# Revit family: Electrical_Equipment-Bridge_Module-HCS-NXHNB_Series
name_source: partatom
category: Data Devices
revit_build: Autodesk Revit 2014 (Build: 20130308_1515(x64)
units: mm (PartAtom-declared; Revit-internal decimal feet)

## types (1)
- NXHNB
    Apparent Load = 0.000 VA
    Assembly Code = D50
    Certifications = Title 24, c UL us
    Connector Description 1 = Power Supply
    Connector Description 2 = Communication
    Construction Housing = GSM UL Rated 94 HB Plastic; Plenum rated Complies with requirements for use in plenum
    DC adjustment range = Rated output voltage: +/-10%
    Default Elevation = 48 "
    Description = Network Bridge Module
    Device Material = Hubbell - Blue
    Electrical Rating Input = 50mA @12/24 volts DC, supplied by room controller SmartPort
    Load Classification = Other
    Manufacturer = Hubbell Control Solutions
    Model = NXHNB Series
    Mounting = Mounts directly to a junction box through an extended 1/2” chase nipple, mechanical only, no electrical connection
    Network = HubbNET, Ethernet IEEE803i, 10BASE-T, PoE Mode B
    Operating Temperature = 0° to 40°
    Power Factor = 1
    Product Documentation Link = https://hubbellcdn.com
    Product Page URL = https://www.hubbell.com
    Relative humidity = 0 to 95%
    Type Comments = Data Devices
    URL = https://www.hubbell.com
    Voltage = 24 V
    Warranty = Five-year limited

## geometry (parser evidence)
native form markers: Sweep x2
no freeform markers — native parametric forms only
